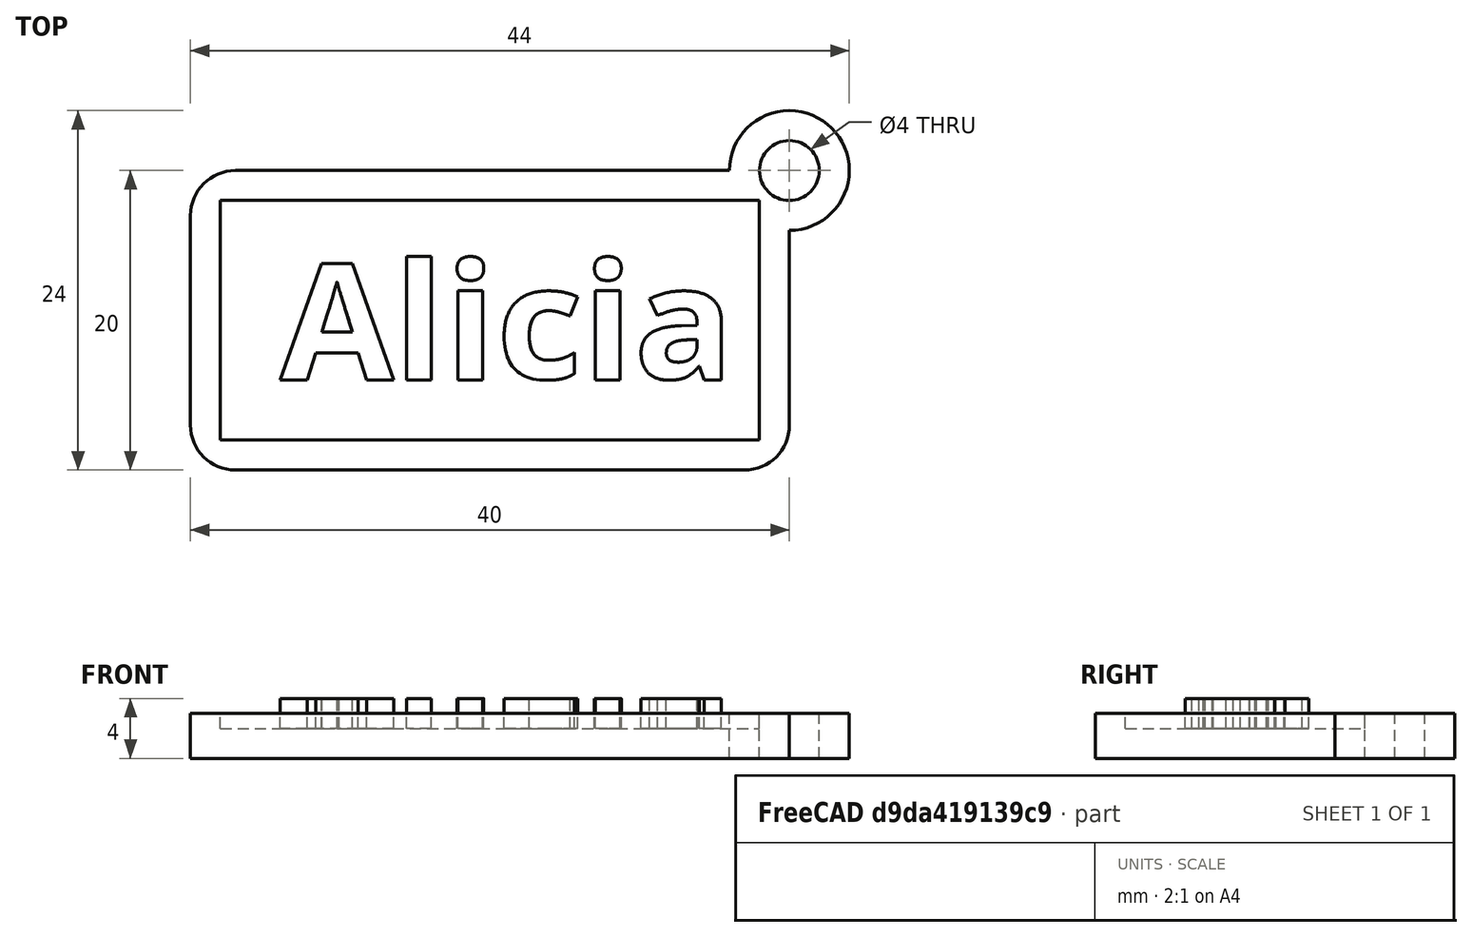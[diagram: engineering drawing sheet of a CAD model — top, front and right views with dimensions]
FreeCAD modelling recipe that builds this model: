
FCSTD DOCUMENT  (FreeCAD 0.17R13217 (Git))
Label: 12-llavero-nombre
License: All rights reserved
LicenseURL: http://en.wikipedia.org/wiki/All_rights_reserved
objects: Part::Box×2, Part::Cylinder×2, Part::MultiFuse×2, Part::Cut×2, Part::Part2DObjectPython×1, Part::Extrusion×1, Part::Fillet×1
note: 11 computed .brp shape members not serialized (recipe doc carries the construction recipe); baked Part::Feature solids carry a one-line shape summary decoded from their .brp

FEATURE [Part::Part2DObjectPython] ShapeString  # Draft 2D object (typed FeaturePython)
  FontFile = <userpath>/develop/CTIF-Madrid-2018-FreeCAD/Sesion-3/OpenSans/OpenSans-Bold.ttf
  Placement = pos=(-14,7,0) rot=(0,0,1;0rad)
  Size = 10
  String = Alicia
  Tracking = 0
FEATURE [Part::Extrusion] Extrude
  Base = -> ShapeString
  Dir = (0,0,1)
  DirMode = 2
  FaceMakerClass = Part::FaceMakerBullseye
  LengthFwd = 3
  LengthRev = 0
  Placement = pos=(0,-1,1) rot=(0,0,1;0rad)
  Solid = false
  Symmetric = false
FEATURE [Part::Box] Box  label="Cubo"
  AttacherType = Attacher::AttachEngine3D
  Height = 3
  Length = 40
  Placement = pos=(-20,0,0) rot=(0,0,1;0rad)
  Width = 20
FEATURE [Part::Box] Box001  label="Cubo001"
  AttacherType = Attacher::AttachEngine3D
  Height = 3
  Length = 36
  Placement = pos=(-18,2,2) rot=(0,0,1;0rad)
  Width = 16
FEATURE [Part::Cylinder] Cylinder  label="Cilindro"
  Angle = 360
  AttacherType = Attacher::AttachEngine3D
  Height = 3
  Placement = pos=(20,20,0) rot=(0,0,1;0rad)
  Radius = 4
FEATURE [Part::MultiFuse] Fusion
  Refine = true
  Shapes = -> [Box,Cylinder]
FEATURE [Part::Cylinder] Cylinder001  label="Cilindro001"
  Angle = 360
  AttacherType = Attacher::AttachEngine3D
  Height = 10
  Placement = pos=(20,20,-4) rot=(0,0,1;0rad)
  Radius = 2
FEATURE [Part::Cut] Cut
  Base = -> Fusion
  Refine = true
  Tool = -> Cylinder001
FEATURE [Part::Cut] Cut001
  Base = -> Cut
  Refine = true
  Tool = -> Box001
FEATURE [Part::MultiFuse] Fusion001
  Refine = true
  Shapes = -> [Extrude,Cut001]
FEATURE [Part::Fillet] Fillet
  Base = -> Fusion001
  Edges = 3 edges r=3: [Edge227,Edge228,Edge234]
